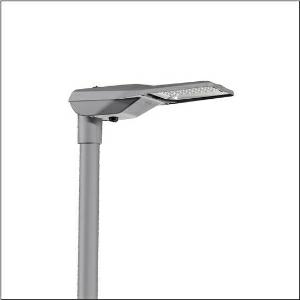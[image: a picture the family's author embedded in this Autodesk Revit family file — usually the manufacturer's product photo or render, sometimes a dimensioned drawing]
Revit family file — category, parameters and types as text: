
# Revit family: streetlight_sl_21_mini___p0_8ab_5xe2r33t08gb_6801
name_source: partatom
category: Lighting Fixtures
units: mm (PartAtom-declared; Revit-internal decimal feet)

## family parameters
Cut with Voids When Loaded = No
Host = Face
Light Source = No
Part Type = Normal
Room Calculation Point = No
Round Connector Dimension = Use Diameter
Shared = No

## types (1)
- --- (1 x LED, 5160 lm, 40.4 W, 3000K)
    Apparent Load = 40 VA
    CIE Flux Codes = 36 71 98 100 100
    Color Rendering = 70
    Color Temperature = 3000K
    Default Elevation = 1800 mm
    Description = Streetlight SL 21 mini, mast luminaire, primary light control with lens, of PMMA, primary optical cover: cover, of toughened safety glass, transparent, light distribution: P0.8aB, light emission: direct distribution, primary light characteristic: asymmetric, installation type: post-top, side-entry, LED, High Power LED, rated luminous flux: 5.160lm, luminous efficacy: 128lm/W, light colour: 730, colour temperature: 3000K, control gear: D4i, control: pre-setting: logarithmic dimming characteristic, flexible luminous flux parameterisation, time-dependent luminous flux control, constant luminous flux control, overheat protection, mains connection: 220..240V, AC, 50/60Hz, start of lifetime: 40W, end of service life: 41W, reduction: 19W, luminaire housing, of diecast aluminium, powder-coated, Siteco® metallic grey (DB 702S), corrosivity category C5 mid according to DIN EN ISO 12944, multi-level sealing system, sealing non-destructively replaceable, inclination adjustable: 0°, 5°, 10°, 15°, please order mast flange separately, length: 628mm, width: 235mm, height: 110mm, mast flange for spigot size: 42mm (side-entry): 5XC10008XM4, 60/48mm (side-entry/post-top): 5XC10108XM2, 76/60mm (side-entry/post-top): 5XC10108XM1, mounting height: 4..8m, Smart Interface below and above, protection rating (complete): IP66, insulation class (complete): insulation class II (safety insulation), certification: CE, ENEC, ENEC+, VDE, impact resistance: IK10, permissible operating ambient temperature for outdoor applications: -40..+50°C, standard-compliant lighting for roads and squares, packaging unit: 1 piece

Light Distribution: P0.8aB
    Height = 110 mm
    Lamp = 1 x LED
    Lamp Light Flux = 5160 lm
    Lamp Power = 40.4 W
    Lamp count = 1
    Length = 625 mm
    Luminous efficacy = 128 lm/W
    Manufacturer = Siteco
    ModVariant = No
    Model = 5XE2R33T08GB
    Number of Poles = 1
    OnlyDefault = Yes
    Power Factor = 1
    Product Name = Streetlight SL 21 mini | P0.8aB
    Product group = mast luminaire | pylon top
    ProductGroupID = 6100
    Protection Class = Protection class II
    Protection Degree = IP 66
    RLX_Detail_Level = 1
    RLX_Emergency_Light_Flux = 0 lm
    RLX_Emergency_Type = 0
    RLX_Emergency_Type_DB = No
    RlxData = <blob elided: 25929 chars, md5=11fa4613>
    Socket = socket
    Standby Power = 0 W
    System Light Flux = 5160 lm
    System Power = 40 W
    Type Comments = factory setting: luminous flux: 100 % | dim-lin: 254 | 812 mA
    Type Image = l_1003514.jpg
    URL = http://relux.com
    VarID = @adj_074598
    Voltage = 0 V
    Weight = 0.00 kg
    Width = 234 mm

## geometry (parser evidence)
native form markers: Blend x4, Sweep x12
no freeform markers — native parametric forms only
